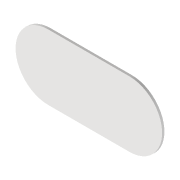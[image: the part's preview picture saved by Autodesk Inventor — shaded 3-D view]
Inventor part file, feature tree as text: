
AUTODESK INVENTOR PART (.ipt)
format: ipt  version: 2021 (Build 250183000, 183)  size: 156,160 bytes
history: native  units: mm
features: other x2, sketch x1, plane x1, extrude x1, reference x1
ambient origin geometry x8: Origin, YZ Plane, XZ Plane, XY Plane, X Axis, Y Axis, Z Axis, Center Point
bodies: Volumenkörper1 (feature_tree)
feature tree (6):
  sketch  "Skizze1"  dims[d0=50.0mm d1=50.0mm d2=62.0mm d3=0.0mm d4=10.0mm d5=0.0mm]
  plane  "Arbeitsebene1"
  extrude  "Extrusion1"  Depth=50.0mm
  reference  "Referenz1"
  other  "Baugruppe1"
  other  "Plenum-Pabst-Lid_V0.3:1"
